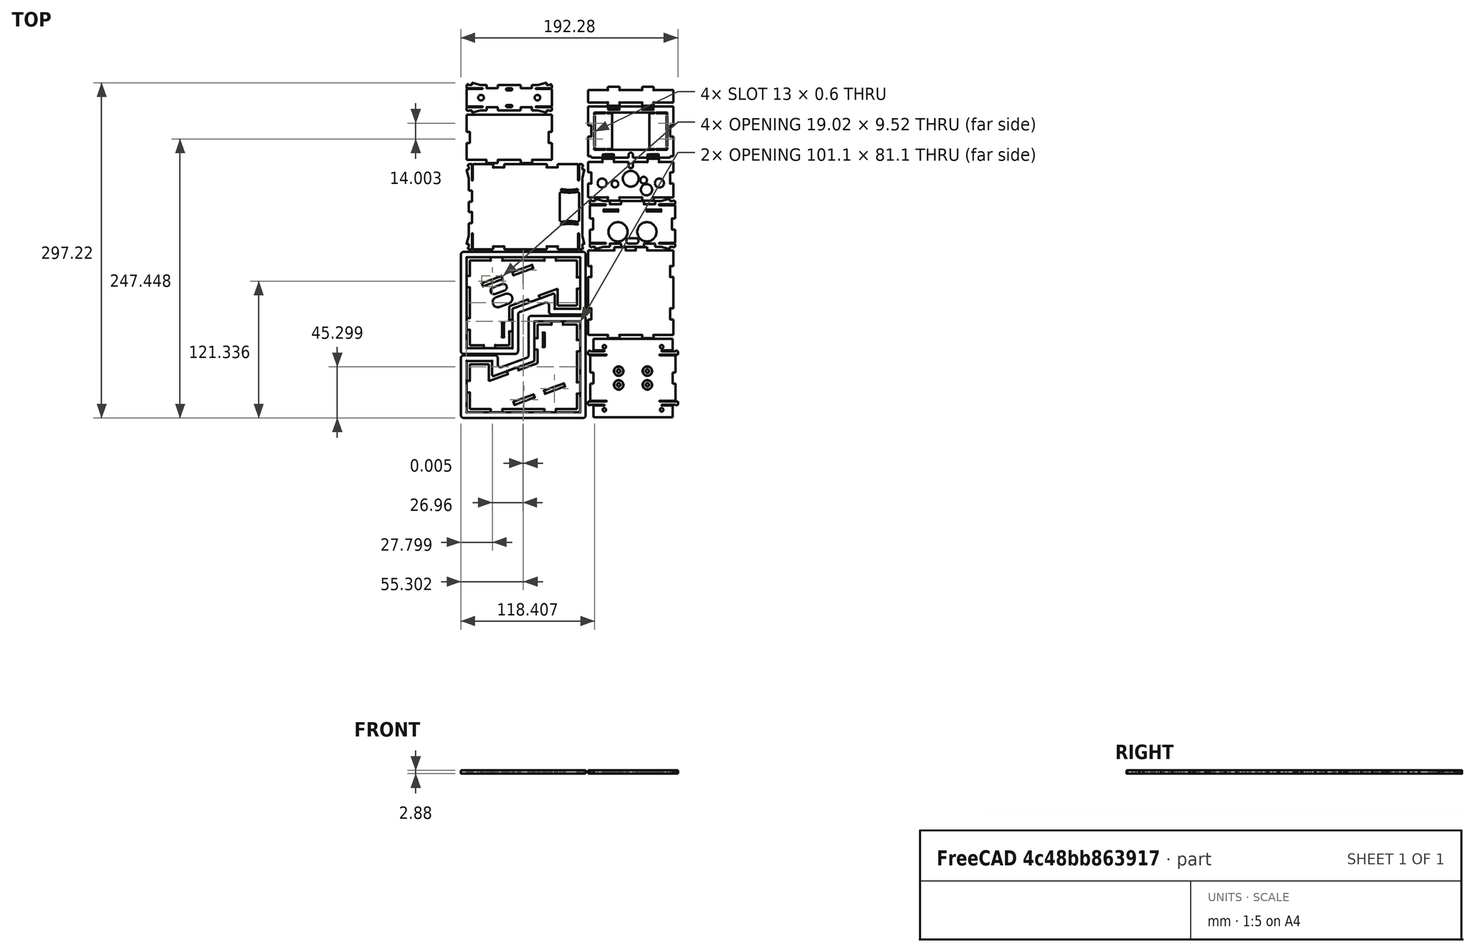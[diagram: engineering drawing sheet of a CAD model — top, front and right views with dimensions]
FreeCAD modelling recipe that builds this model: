
FCSTD DOCUMENT  (FreeCAD 1.0R39109 (Git))
Label: TheThing_v5_tabs_export
License: All rights reserved
LicenseURL: http://www.ohwr.org/attachments/2388/cern_ohl_v_1_2.txt
objects: Part::Part2DObjectPython×14, Part::Feature×13, Sketcher::SketchObject×1
note: 29 computed .brp shape members not serialized (recipe doc carries the construction recipe); baked Part::Feature solids carry a one-line shape summary decoded from their .brp

FEATURE [Part::Feature] test
  Placement = pos=(0,0,0) rot=(0,1,0;1.5708rad)
  shape: bbox 100.6 x 80.6 x 2.8 mm, 106 faces (baked)
FEATURE [Part::Feature] test001
  Placement = pos=(25.655,-97,-72.8) rot=(0.707107,0,-0.707107;3.14159rad)
  shape: bbox 100.6 x 80.6 x 2.8 mm, 96 faces (baked)
FEATURE [Part::Feature] test002
  Placement = pos=(110,-87,-32.2) rot=(-0.939693,0,0;1.22173rad)
  shape: bbox 79.6 x 69.38 x 2.8 mm, 110 faces (baked)
FEATURE [Part::Feature] test003
  Placement = pos=(0.33,129.2,25.33) rot=(0,-1,0;3.14159rad)
  shape: bbox 75.6 x 42.8 x 2.8 mm, 30 faces (baked)
FEATURE [Part::Feature] test004
  Placement = pos=(108,9,-0.3) rot=(0,0,1;0rad)
  shape: bbox 75.6 x 80.6 x 2.8 mm, 54 faces (baked)
FEATURE [Part::Feature] test005
  Placement = pos=(108,131,-38.1) rot=(0,0,1;0rad)
  shape: bbox 75.6 x 36.97 x 2.8 mm, 52 faces (baked)
FEATURE [Part::Feature] test006
  Placement = pos=(108,146,5.5) rot=(1,0,0;3.14159rad)
  shape: bbox 75.6 x 16.6 x 2.8 mm, 30 faces (baked)
FEATURE [Part::Feature] test007
  Placement = pos=(1.86,65,-55.2) rot=(0.57735,0.57735,0.57735;2.0944rad)
  shape: bbox 104.4 x 75.6 x 2.8 mm, 112 faces (baked)
FEATURE [Part::Feature] test008
  Placement = pos=(109.5,67,22.6) rot=(0,0.707107,0.707107;3.14159rad)
  shape: bbox 75.6 x 44.36 x 2.8 mm, 116 faces (baked)
FEATURE [Part::Feature] test009
  Placement = pos=(0.3,110,-60.36) rot=(-1,0,0;1.5708rad)
  shape: bbox 75.6 x 26.36 x 2.8 mm, 92 faces (baked)
FEATURE [Part::Feature] test010
  Placement = pos=(108,117,-59.7) rot=(-0.939693,0,0;1.22173rad)
  shape: bbox 75.6 x 45.69 x 2.923 mm, 114 faces (baked)
FEATURE [Part::Feature] test011
  Placement = pos=(0,0,-2) rot=(0,-1,0;4.71239rad)
  shape: bbox 110.6 x 90.6 x 2.8 mm, 46 faces (baked)
FEATURE [Part::Feature] test012
  Placement = pos=(25.65,-97,-2) rot=(0.707107,0,-0.707107;3.14159rad)
  shape: bbox 110.6 x 90.6 x 2.8 mm, 46 faces (baked)
FEATURE [Part::Part2DObjectPython] Shape2DView  # Draft 2D object (typed FeaturePython)
  AutoUpdate = true
  Base = -> test
  Clip = false
  FuseArch = false
  HiddenLines = false
  InPlace = true
  OnlySolids = false
  Projection = (0,0,1)
  ProjectionMode = 0
  SegmentLength = 0.05
  Tessellation = false
  VisibleOnly = false
FEATURE [Part::Part2DObjectPython] Shape2DView001  # Draft 2D object (typed FeaturePython)
  AutoUpdate = true
  Base = -> test001
  Clip = false
  FuseArch = false
  HiddenLines = false
  InPlace = true
  OnlySolids = false
  Projection = (0,0,1)
  ProjectionMode = 0
  SegmentLength = 0.05
  Tessellation = false
  VisibleOnly = false
FEATURE [Part::Part2DObjectPython] Shape2DView002  # Draft 2D object (typed FeaturePython)
  AutoUpdate = true
  Base = -> test002
  Clip = false
  FuseArch = false
  HiddenLines = false
  InPlace = true
  OnlySolids = false
  Projection = (0,0,1)
  ProjectionMode = 0
  SegmentLength = 0.05
  Tessellation = false
  VisibleOnly = false
FEATURE [Part::Part2DObjectPython] Shape2DView003  # Draft 2D object (typed FeaturePython)
  AutoUpdate = true
  Base = -> test003
  Clip = false
  FuseArch = false
  HiddenLines = false
  InPlace = true
  OnlySolids = false
  Projection = (0,0,1)
  ProjectionMode = 0
  SegmentLength = 0.05
  Tessellation = false
  VisibleOnly = false
FEATURE [Part::Part2DObjectPython] Shape2DView004  # Draft 2D object (typed FeaturePython)
  AutoUpdate = true
  Base = -> test004
  Clip = false
  FuseArch = false
  HiddenLines = false
  InPlace = true
  OnlySolids = false
  Projection = (0,0,1)
  ProjectionMode = 0
  SegmentLength = 0.05
  Tessellation = false
  VisibleOnly = false
FEATURE [Part::Part2DObjectPython] Shape2DView005  # Draft 2D object (typed FeaturePython)
  AutoUpdate = true
  Base = -> test005
  Clip = false
  FuseArch = false
  HiddenLines = false
  InPlace = true
  OnlySolids = false
  Projection = (0,0,1)
  ProjectionMode = 0
  SegmentLength = 0.05
  Tessellation = false
  VisibleOnly = false
FEATURE [Part::Part2DObjectPython] Shape2DView006  # Draft 2D object (typed FeaturePython)
  AutoUpdate = true
  Base = -> test006
  Clip = false
  FuseArch = false
  HiddenLines = false
  InPlace = true
  OnlySolids = false
  Projection = (0,0,1)
  ProjectionMode = 0
  SegmentLength = 0.05
  Tessellation = false
  VisibleOnly = false
FEATURE [Part::Part2DObjectPython] Shape2DView007  # Draft 2D object (typed FeaturePython)
  AutoUpdate = true
  Base = -> test007
  Clip = false
  FuseArch = false
  HiddenLines = false
  InPlace = true
  OnlySolids = false
  Projection = (0,0,1)
  ProjectionMode = 0
  SegmentLength = 0.05
  Tessellation = false
  VisibleOnly = false
FEATURE [Part::Part2DObjectPython] Shape2DView008  # Draft 2D object (typed FeaturePython)
  AutoUpdate = true
  Base = -> test008
  Clip = false
  FuseArch = false
  HiddenLines = false
  InPlace = true
  OnlySolids = false
  Projection = (0,0,1)
  ProjectionMode = 0
  SegmentLength = 0.05
  Tessellation = false
  VisibleOnly = false
FEATURE [Part::Part2DObjectPython] Shape2DView009  # Draft 2D object (typed FeaturePython)
  AutoUpdate = true
  Base = -> test009
  Clip = false
  FuseArch = false
  HiddenLines = false
  InPlace = true
  OnlySolids = false
  Projection = (0,0,1)
  ProjectionMode = 0
  SegmentLength = 0.05
  Tessellation = false
  VisibleOnly = false
FEATURE [Part::Part2DObjectPython] Shape2DView010  # Draft 2D object (typed FeaturePython)
  AutoUpdate = true
  Base = -> test010
  Clip = false
  FuseArch = false
  HiddenLines = false
  InPlace = true
  OnlySolids = false
  Projection = (0,0,1)
  ProjectionMode = 0
  SegmentLength = 0.05
  Tessellation = false
  VisibleOnly = false
FEATURE [Part::Part2DObjectPython] Shape2DView011  # Draft 2D object (typed FeaturePython)
  AutoUpdate = true
  Base = -> test011
  Clip = false
  FuseArch = false
  HiddenLines = false
  InPlace = true
  OnlySolids = false
  Projection = (0,0,1)
  ProjectionMode = 0
  SegmentLength = 0.05
  Tessellation = false
  VisibleOnly = false
FEATURE [Part::Part2DObjectPython] Shape2DView012  # Draft 2D object (typed FeaturePython)
  AutoUpdate = true
  Base = -> test012
  Clip = false
  FuseArch = false
  HiddenLines = false
  InPlace = true
  OnlySolids = false
  Projection = (0,0,1)
  ProjectionMode = 0
  SegmentLength = 0.05
  Tessellation = false
  VisibleOnly = false
FEATURE [Sketcher::SketchObject] Sketch
  ArcFitTolerance = 1e-06
  FullyConstrained = true
  MakeInternals = false
  sketch-geometry (104):
    g0: LineSegment StartX=70.2 StartY=225.92 StartZ=0 EndX=87.9733 EndY=225.92 EndZ=0
    g1: LineSegment StartX=97.7866 StartY=225.92 StartZ=0 EndX=118.213 EndY=225.92 EndZ=0
    g2: LineSegment StartX=128.027 StartY=225.92 StartZ=0 EndX=145.8 EndY=225.92 EndZ=0
    g3: LineSegment StartX=73 StartY=181.92 StartZ=0 EndX=70.2 EndY=181.92 EndZ=0
    g4: LineSegment StartX=73 StartY=180.52 StartZ=0 EndX=73 EndY=181.92 EndZ=0
    g5: LineSegment StartX=83.1933 StartY=180.52 StartZ=0 EndX=73 EndY=180.52 EndZ=0
    g6: LineSegment StartX=83.1933 StartY=180.52 StartZ=0 EndX=83.1933 EndY=183.089 EndZ=0
    g7: LineSegment StartX=83.4641 StartY=183.37 StartZ=0 EndX=92.7432 EndY=183.37 EndZ=0
    g8: LineSegment StartX=93.0066 StartY=180.52 StartZ=0 EndX=93.0066 EndY=183.089 EndZ=0
    g9: LineSegment StartX=106 StartY=180.52 StartZ=0 EndX=93.0066 EndY=180.52 EndZ=0
    g10: LineSegment StartX=106 StartY=183.02 StartZ=0 EndX=106 EndY=180.52 EndZ=0
    g11: ArcOfCircle CenterX=108 CenterY=183.02 CenterZ=0 NormalX=0 NormalY=0 NormalZ=1 AngleXU=0 Radius=2 StartAngle=0 EndAngle=3.14159
    g12: LineSegment StartX=110 StartY=180.52 StartZ=0 EndX=110 EndY=183.02 EndZ=0
    g13: LineSegment StartX=122.993 StartY=180.52 StartZ=0 EndX=110 EndY=180.52 EndZ=0
    g14: LineSegment StartX=122.993 StartY=180.52 StartZ=0 EndX=122.993 EndY=183.089 EndZ=0
    g15: LineSegment StartX=123.264 StartY=183.37 StartZ=0 EndX=132.536 EndY=183.37 EndZ=0
    g16: LineSegment StartX=132.807 StartY=180.52 StartZ=0 EndX=132.807 EndY=183.089 EndZ=0
    g17: LineSegment StartX=143 StartY=180.52 StartZ=0 EndX=132.807 EndY=180.52 EndZ=0
    g18: LineSegment StartX=143 StartY=181.92 StartZ=0 EndX=143 EndY=180.52 EndZ=0
    g19: LineSegment StartX=145.8 StartY=181.92 StartZ=0 EndX=143 EndY=181.92 EndZ=0
    g20: LineSegment StartX=145.8 StartY=199.333 StartZ=0 EndX=145.8 EndY=181.92 EndZ=0
    g21: LineSegment StartX=143.225 StartY=199.333 StartZ=0 EndX=145.8 EndY=199.333 EndZ=0
    g22: ArcOfCircle CenterX=143.053 CenterY=199.432 CenterZ=0 NormalX=0 NormalY=0 NormalZ=1 AngleXU=0 Radius=0.19911 StartAngle=2.0944 EndAngle=5.75959
    g23: LineSegment StartX=142.953 StartY=208.874 StartZ=0 EndX=142.953 EndY=199.605 EndZ=0
    g24: ArcOfCircle CenterX=143.053 CenterY=209.046 CenterZ=0 NormalX=0 NormalY=0 NormalZ=1 AngleXU=0 Radius=0.19911 StartAngle=0.5236 EndAngle=4.18879
    g25: LineSegment StartX=143.225 StartY=209.146 StartZ=0 EndX=145.8 EndY=209.146 EndZ=0
    g26: LineSegment StartX=145.8 StartY=225.92 StartZ=0 EndX=145.8 EndY=209.146 EndZ=0
    g27: LineSegment StartX=128.027 StartY=225.92 StartZ=0 EndX=128.027 EndY=223.36 EndZ=0
    g28: LineSegment StartX=118.514 StartY=223.12 StartZ=0 EndX=127.726 EndY=223.12 EndZ=0
    g29: LineSegment StartX=118.213 StartY=225.92 StartZ=0 EndX=118.213 EndY=223.36 EndZ=0
    g30: LineSegment StartX=97.7866 StartY=225.92 StartZ=0 EndX=97.7866 EndY=223.36 EndZ=0
    g31: LineSegment StartX=88.274 StartY=223.121 StartZ=0 EndX=97.486 EndY=223.121 EndZ=0
    g32: LineSegment StartX=87.9733 StartY=225.92 StartZ=0 EndX=87.9733 EndY=223.36 EndZ=0
    g33: LineSegment StartX=70.2 StartY=209.146 StartZ=0 EndX=70.2 EndY=225.92 EndZ=0
    g34: LineSegment StartX=70.2 StartY=209.146 StartZ=0 EndX=72.7636 EndY=209.146 EndZ=0
    g35: LineSegment StartX=73.0466 StartY=208.863 StartZ=0 EndX=73.0466 EndY=199.627 EndZ=0
    g36: LineSegment StartX=70.2 StartY=199.333 StartZ=0 EndX=72.7747 EndY=199.333 EndZ=0
    g37: LineSegment StartX=70.2 StartY=181.92 StartZ=0 EndX=70.2 EndY=199.333 EndZ=0
    g38: ArcOfCircle CenterX=75.927 CenterY=188.039 CenterZ=0 NormalX=0 NormalY=0 NormalZ=1 AngleXU=-9e-16 Radius=0.3 StartAngle=3.14159 EndAngle=4.71239
    g39: LineSegment StartX=75.927 StartY=187.739 StartZ=0 EndX=85.3256 EndY=187.739 EndZ=0
    g40: LineSegment StartX=75.627 StartY=189.438 StartZ=0 EndX=75.627 EndY=188.039 EndZ=0
    g41: ArcOfCircle CenterX=85.3256 CenterY=188.039 CenterZ=0 NormalX=0 NormalY=0 NormalZ=1 AngleXU=-9e-16 Radius=0.3 StartAngle=4.71239 EndAngle=7.85398
    g42: ArcOfCircle CenterX=75.927 CenterY=189.438 CenterZ=0 NormalX=0 NormalY=0 NormalZ=1 AngleXU=-9e-16 Radius=0.3 StartAngle=-5.3e-15 EndAngle=3.14159
    g43: LineSegment StartX=85.3256 StartY=188.339 StartZ=0 EndX=76.227 EndY=188.339 EndZ=0
    g44: LineSegment StartX=76.227 StartY=188.339 StartZ=0 EndX=76.227 EndY=189.438 EndZ=0
    g45: ArcOfCircle CenterX=75.927 CenterY=191.038 CenterZ=0 NormalX=0 NormalY=0 NormalZ=1 AngleXU=-9e-16 Radius=0.3 StartAngle=3.14159 EndAngle=6.28319
    g46: LineSegment StartX=76.227 StartY=191.038 StartZ=0 EndX=76.227 EndY=203.438 EndZ=0
    g47: LineSegment StartX=75.627 StartY=191.038 StartZ=0 EndX=75.627 EndY=203.438 EndZ=0
    g48: ArcOfCircle CenterX=75.927 CenterY=203.438 CenterZ=0 NormalX=0 NormalY=0 NormalZ=1 AngleXU=-9e-16 Radius=0.3 StartAngle=-3.6e-15 EndAngle=3.14159
    g49: LineSegment StartX=76.227 StartY=217.441 StartZ=0 EndX=76.227 EndY=205.041 EndZ=0
    g50: ArcOfCircle CenterX=75.927 CenterY=217.441 CenterZ=0 NormalX=0 NormalY=0 NormalZ=1 AngleXU=0 Radius=0.3 StartAngle=-4.4e-15 EndAngle=3.14159
    g51: ArcOfCircle CenterX=75.927 CenterY=205.041 CenterZ=0 NormalX=0 NormalY=0 NormalZ=1 AngleXU=0 Radius=0.3 StartAngle=3.14159 EndAngle=6.28319
    g52: LineSegment StartX=75.627 StartY=217.441 StartZ=0 EndX=75.627 EndY=205.041 EndZ=0
    g53: LineSegment StartX=75.927 StartY=220.739 StartZ=0 EndX=85.3256 EndY=220.739 EndZ=0
    g54: ArcOfCircle CenterX=75.927 CenterY=220.439 CenterZ=0 NormalX=0 NormalY=0 NormalZ=1 AngleXU=0 Radius=0.3 StartAngle=1.5708 EndAngle=3.14159
    g55: ArcOfCircle CenterX=85.3256 CenterY=220.439 CenterZ=0 NormalX=0 NormalY=0 NormalZ=1 AngleXU=0 Radius=0.3 StartAngle=4.71239 EndAngle=7.85398
    g56: LineSegment StartX=75.627 StartY=219.041 StartZ=0 EndX=75.627 EndY=220.439 EndZ=0
    g57: LineSegment StartX=85.3256 StartY=220.139 StartZ=0 EndX=76.227 EndY=220.139 EndZ=0
    g58: ArcOfCircle CenterX=75.927 CenterY=219.041 CenterZ=0 NormalX=0 NormalY=0 NormalZ=1 AngleXU=0 Radius=0.3 StartAngle=3.14159 EndAngle=6.28319
    g59: LineSegment StartX=76.227 StartY=220.139 StartZ=0 EndX=76.227 EndY=219.041 EndZ=0
    g60: ArcOfCircle CenterX=129.074 CenterY=220.439 CenterZ=0 NormalX=0 NormalY=0 NormalZ=1 AngleXU=-3.14159 Radius=0.3 StartAngle=1.5708 EndAngle=4.71239
    g61: LineSegment StartX=86.9256 StartY=220.739 StartZ=0 EndX=129.074 EndY=220.739 EndZ=0
    g62: LineSegment StartX=124.501 StartY=220.139 StartZ=0 EndX=129.074 EndY=220.139 EndZ=0
    g63: ArcOfCircle CenterX=86.9256 CenterY=220.439 CenterZ=0 NormalX=0 NormalY=0 NormalZ=1 AngleXU=0 Radius=0.3 StartAngle=1.5708 EndAngle=4.71239
    g64: LineSegment StartX=124.501 StartY=220.139 StartZ=0 EndX=124.501 EndY=188.339 EndZ=0
    g65: LineSegment StartX=91.4993 StartY=220.139 StartZ=0 EndX=86.9256 EndY=220.139 EndZ=0
    g66: LineSegment StartX=124.501 StartY=188.339 StartZ=0 EndX=129.074 EndY=188.339 EndZ=0
    g67: LineSegment StartX=91.4993 StartY=188.339 StartZ=0 EndX=91.4993 EndY=220.139 EndZ=0
    g68: ArcOfCircle CenterX=129.074 CenterY=188.039 CenterZ=0 NormalX=0 NormalY=0 NormalZ=1 AngleXU=3.14159 Radius=0.3 StartAngle=1.5708 EndAngle=4.71239
    g69: LineSegment StartX=91.4993 StartY=188.339 StartZ=0 EndX=86.9256 EndY=188.339 EndZ=0
    g70: LineSegment StartX=129.074 StartY=187.739 StartZ=0 EndX=86.9256 EndY=187.739 EndZ=0
    g71: ArcOfCircle CenterX=86.9256 CenterY=188.039 CenterZ=0 NormalX=0 NormalY=0 NormalZ=1 AngleXU=-9e-16 Radius=0.3 StartAngle=1.5708 EndAngle=4.71239
    g72: LineSegment StartX=140.073 StartY=187.739 StartZ=0 EndX=130.674 EndY=187.739 EndZ=0
    g73: ArcOfCircle CenterX=140.073 CenterY=188.039 CenterZ=0 NormalX=0 NormalY=0 NormalZ=1 AngleXU=3.14159 Radius=0.3 StartAngle=1.5708 EndAngle=3.14159
    g74: ArcOfCircle CenterX=130.674 CenterY=188.039 CenterZ=0 NormalX=0 NormalY=0 NormalZ=1 AngleXU=3.14159 Radius=0.3 StartAngle=4.71239 EndAngle=7.85398
    g75: LineSegment StartX=140.373 StartY=189.438 StartZ=0 EndX=140.373 EndY=188.039 EndZ=0
    g76: LineSegment StartX=130.674 StartY=188.339 StartZ=0 EndX=139.773 EndY=188.339 EndZ=0
    g77: ArcOfCircle CenterX=140.073 CenterY=189.438 CenterZ=0 NormalX=0 NormalY=0 NormalZ=1 AngleXU=3.14159 Radius=0.3 StartAngle=3.14159 EndAngle=6.28319
    g78: LineSegment StartX=139.773 StartY=188.339 StartZ=0 EndX=139.773 EndY=189.438 EndZ=0
    g79: LineSegment StartX=139.773 StartY=191.038 StartZ=0 EndX=139.773 EndY=203.438 EndZ=0
    g80: ArcOfCircle CenterX=140.073 CenterY=191.038 CenterZ=0 NormalX=0 NormalY=0 NormalZ=1 AngleXU=3.14159 Radius=0.3 StartAngle=-4.4e-15 EndAngle=3.14159
    g81: ArcOfCircle CenterX=140.073 CenterY=203.438 CenterZ=0 NormalX=0 NormalY=0 NormalZ=1 AngleXU=3.14159 Radius=0.3 StartAngle=3.14159 EndAngle=6.28319
    g82: LineSegment StartX=140.373 StartY=191.038 StartZ=0 EndX=140.373 EndY=203.438 EndZ=0
    g83: ArcOfCircle CenterX=140.073 CenterY=217.441 CenterZ=0 NormalX=0 NormalY=0 NormalZ=1 AngleXU=-3.14159 Radius=0.3 StartAngle=3.14159 EndAngle=6.28319
    g84: LineSegment StartX=139.773 StartY=217.441 StartZ=0 EndX=139.773 EndY=205.041 EndZ=0
    g85: LineSegment StartX=140.373 StartY=217.441 StartZ=0 EndX=140.373 EndY=205.041 EndZ=0
    g86: ArcOfCircle CenterX=140.073 CenterY=205.041 CenterZ=0 NormalX=0 NormalY=0 NormalZ=1 AngleXU=-3.14159 Radius=0.3 StartAngle=-3.6e-15 EndAngle=3.14159
    g87: ArcOfCircle CenterX=140.073 CenterY=220.439 CenterZ=0 NormalX=0 NormalY=0 NormalZ=1 AngleXU=-3.14159 Radius=0.3 StartAngle=3.14159 EndAngle=4.71239
    g88: LineSegment StartX=140.073 StartY=220.739 StartZ=0 EndX=130.674 EndY=220.739 EndZ=0
    g89: LineSegment StartX=140.373 StartY=219.041 StartZ=0 EndX=140.373 EndY=220.439 EndZ=0
    g90: ArcOfCircle CenterX=130.674 CenterY=220.439 CenterZ=0 NormalX=0 NormalY=0 NormalZ=1 AngleXU=-3.14159 Radius=0.3 StartAngle=4.71239 EndAngle=7.85398
    g91: ArcOfCircle CenterX=140.073 CenterY=219.041 CenterZ=0 NormalX=0 NormalY=0 NormalZ=1 AngleXU=-3.14159 Radius=0.3 StartAngle=-5.3e-15 EndAngle=3.14159
    g92: LineSegment StartX=130.674 StartY=220.139 StartZ=0 EndX=139.773 EndY=220.139 EndZ=0
    g93: LineSegment StartX=139.773 StartY=220.139 StartZ=0 EndX=139.773 EndY=219.041 EndZ=0
    g94: ArcOfCircle CenterX=97.6871 CenterY=223.177 CenterZ=0 NormalX=0 NormalY=0 NormalZ=1 AngleXU=0 Radius=0.208767 StartAngle=3.41408 EndAngle=7.35689
    g95: ArcOfCircle CenterX=88.0729 CenterY=223.177 CenterZ=0 NormalX=0 NormalY=0 NormalZ=1 AngleXU=0 Radius=0.208767 StartAngle=2.06789 EndAngle=6.0107
    g96: ArcOfCircle CenterX=118.313 CenterY=223.177 CenterZ=0 NormalX=0 NormalY=0 NormalZ=1 AngleXU=0 Radius=0.208767 StartAngle=2.06789 EndAngle=6.00866
    g97: ArcOfCircle CenterX=127.927 CenterY=223.177 CenterZ=0 NormalX=0 NormalY=0 NormalZ=1 AngleXU=0 Radius=0.208767 StartAngle=3.41612 EndAngle=7.35689
    g98: ArcOfCircle CenterX=72.9471 CenterY=209.046 CenterZ=0 NormalX=0 NormalY=0 NormalZ=1 AngleXU=0 Radius=0.208767 StartAngle=5.20948 EndAngle=8.92769
    g99: ArcOfCircle CenterX=72.9541 CenterY=199.439 CenterZ=0 NormalX=0 NormalY=0 NormalZ=1 AngleXU=0 Radius=0.208767 StartAngle=3.67768 EndAngle=7.39491
    g100: ArcOfCircle CenterX=83.2898 CenterY=183.267 CenterZ=0 NormalX=0 NormalY=0 NormalZ=1 AngleXU=0 Radius=0.202242 StartAngle=0.532255 EndAngle=4.2153
    g101: ArcOfCircle CenterX=92.9102 CenterY=183.263 CenterZ=0 NormalX=0 NormalY=0 NormalZ=1 AngleXU=0 Radius=0.19839 StartAngle=5.22004 EndAngle=8.85496
    g102: ArcOfCircle CenterX=123.09 CenterY=183.267 CenterZ=0 NormalX=0 NormalY=0 NormalZ=1 AngleXU=0 Radius=0.202242 StartAngle=0.532259 EndAngle=4.2153
    g103: ArcOfCircle CenterX=132.71 CenterY=183.267 CenterZ=0 NormalX=0 NormalY=0 NormalZ=1 AngleXU=0 Radius=0.202242 StartAngle=5.20948 EndAngle=8.89252
  constraints (299):
    c: Coincident(g2,g27)
    c: Coincident(g2,g26)
    c: Coincident(g25,g26)
    c: Coincident(g24,g25)
    c: Coincident(g23,g24)
    c: Coincident(g22,g23)
    c: Coincident(g21,g22)
    c: Coincident(g20,g21)
    c: Coincident(g19,g20)
    c: Coincident(g18,g19)
    c: Coincident(g17,g18)
    c: Coincident(g12,g13)
    c: Coincident(g9,g10)
    c: Coincident(g4,g5)
    c: Coincident(g3,g4)
    c: Coincident(g3,g37)
    c: Coincident(g36,g37)
    c: Coincident(g33,g34)
    c: Coincident(g0,g33)
    c: Coincident(g0,g32)
    c: Coincident(g1,g30)
    c: Coincident(g1,g29)
    c: Vertical(g27)
    c: Horizontal(g2)
    c: Vertical(g26)
    c: Horizontal(g25)
    c: Vertical(g23)
    c: Horizontal(g21)
    c: Vertical(g20)
    c: Horizontal(g19)
    c: Vertical(g18)
    c: Horizontal(g17)
    c: Vertical(g16)
    c: Horizontal(g15)
    c: Vertical(g14)
    c: Horizontal(g13)
    c: Vertical(g12)
    c: Vertical(g10)
    c: Horizontal(g9)
    c: Vertical(g8)
    c: Horizontal(g7)
    c: Vertical(g6)
    c: Horizontal(g5)
    c: Vertical(g4)
    c: Horizontal(g3)
    c: Vertical(g37)
    c: Horizontal(g36)
    c: Vertical(g35)
    c: Horizontal(g34)
    c: Vertical(g33)
    c: Horizontal(g0)
    c: Vertical(g32)
    c: Horizontal(g31)
    c: Vertical(g30)
    c: Horizontal(g1)
    c: Vertical(g29)
    c: Horizontal(g28)
    c: Vertical(g56)
    c: Vertical(g59)
    c: Horizontal(g57)
    c: Horizontal(g53)
    c: Horizontal(g65)
    c: Horizontal(g61)
    c: Vertical(g67)
    c: Horizontal(g62)
    c: Vertical(g64)
    c: Horizontal(g88)
    c: Horizontal(g92)
    c: Vertical(g93)
    c: Vertical(g89)
    c: Vertical(g84)
    c: Vertical(g85)
    c: Vertical(g79)
    c: Vertical(g82)
    c: Vertical(g78)
    c: Vertical(g75)
    c: Horizontal(g76)
    c: Horizontal(g72)
    c: Horizontal(g66)
    c: Horizontal(g70)
    c: Horizontal(g69)
    c: Horizontal(g43)
    c: Horizontal(g39)
    c: Vertical(g44)
    c: Vertical(g40)
    c: Vertical(g47)
    c: Vertical(g46)
    c: Vertical(g49)
    c: Vertical(g52)
    c: Coincident(g57,g59)
    c: Coincident(g62,g64)
    c: Coincident(g64,g66)
    c: Coincident(g67,g69)
    c: Coincident(g65,g67)
    c: Coincident(g92,g93)
    c: Coincident(g76,g78)
    c: Coincident(g43,g44)
    c: DistanceX(g58) = 75.927
    c: DistanceY(g58) = 219.041
    c: DistanceX(g54) = 75.927
    c: DistanceY(g54) = 220.439
    c: DistanceX(g55) = 85.3256
    c: DistanceY(g55) = 220.439
    c: DistanceX(g63) = 86.9256
    c: DistanceY(g63) = 220.439
    c: DistanceX(g60) = 129.074
    c: DistanceY(g60) = 220.439
    c: DistanceX(g90) = 130.674
    c: DistanceY(g90) = 220.439
    c: DistanceX(g87) = 140.073
    c: DistanceY(g87) = 220.439
    c: DistanceX(g91) = 140.073
    c: DistanceY(g91) = 219.041
    c: DistanceX(g83) = 140.073
    c: DistanceY(g83) = 217.441
    c: DistanceX(g81) = 140.073
    c: DistanceY(g81) = 203.438
    c: DistanceX(g77) = 140.073
    c: DistanceY(g77) = 189.438
    c: DistanceX(g73) = 140.073
    c: DistanceY(g73) = 188.039
    c: DistanceX(g74) = 130.674
    c: DistanceY(g74) = 188.039
    c: DistanceX(g68) = 129.074
    c: DistanceY(g68) = 188.039
    c: DistanceX(g11) = 108
    c: DistanceY(g11) = 183.02
    c: DistanceX(g71) = 86.9256
    c: DistanceY(g71) = 188.039
    c: DistanceX(g41) = 85.3256
    c: DistanceY(g41) = 188.039
    c: DistanceX(g38) = 75.927
    c: DistanceY(g38) = 188.039
    c: DistanceX(g42) = 75.927
    c: DistanceY(g42) = 189.438
    c: DistanceX(g45) = 75.927
    c: DistanceY(g45) = 191.038
    c: DistanceX(g51) = 75.927
    c: DistanceY(g51) = 205.041
    c: DistanceX(g0) = 70.2
    c: DistanceY(g0) = 225.92
    c: DistanceX(g32) = 87.9733
    c: DistanceY(g32) = 223.36
    c: DistanceX(g30) = 97.7866
    c: DistanceY(g30) = 223.36
    c: DistanceX(g1) = 118.213
    c: DistanceY(g1) = 225.92
    c: DistanceX(g27) = 128.027
    c: DistanceY(g27) = 223.36
    c: DistanceX(g2) = 145.8
    c: DistanceY(g2) = 225.92
    c: DistanceX(g24) = 143.225
    c: DistanceY(g24) = 209.146
    c: DistanceX(g24) = 143.053
    c: DistanceY(g24) = 209.046
    c: DistanceX(g22) = 142.953
    c: DistanceY(g22) = 199.605
    c: DistanceX(g22) = 143.053
    c: DistanceY(g22) = 199.432
    c: DistanceX(g20) = 145.8
    c: DistanceY(g20) = 199.333
    c: DistanceX(g18) = 143
    c: DistanceY(g18) = 181.92
    c: DistanceX(g16) = 132.807
    c: DistanceY(g16) = 183.089
    c: DistanceX(g14) = 122.993
    c: DistanceY(g14) = 183.089
    c: DistanceX(g12) = 110
    c: DistanceY(g12) = 180.52
    c: DistanceY(g9) = 180.52
    c: DistanceX(g8) = 93.0066
    c: DistanceY(g8) = 183.089
    c: DistanceX(g7) = 92.7432
    c: DistanceY(g7) = 183.37
    c: DistanceX(g6) = 83.1933
    c: DistanceY(g6) = 183.089
    c: DistanceX(g4) = 73
    c: DistanceY(g4) = 180.52
    c: DistanceX(g3) = 70.2
    c: DistanceY(g3) = 181.92
    c: DistanceX(g36) = 72.7747
    c: DistanceY(g36) = 199.333
    c: DistanceX(g35) = 73.0466
    c: Equal(g4,g18)
    c: Equal(g33,g26)
    c: Coincident(g16,g17)
    c: Coincident(g13,g14)
    c: Tangent(g11,g12) = -1.5708
    c: Tangent(g10,g11) = -1.5708
    c: Coincident(g8,g9)
    c: Coincident(g5,g6)
    c: Tangent(g56,g58) = 1.5708
    c: Tangent(g58,g59) = 1.5708
    c: Tangent(g54,g56) = 1.5708
    c: Tangent(g53,g54) = 1.5708
    c: Tangent(g53,g55) = 1.5708
    c: Tangent(g55,g57) = 1.5708
    c: Tangent(g61,g63) = 1.5708
    c: Tangent(g63,g65) = 1.5708
    c: Tangent(g60,g61) = 1.5708
    c: Tangent(g60,g62) = -1.5708
    c: Tangent(g88,g90) = -1.5708
    c: Tangent(g90,g92) = -1.5708
    c: Tangent(g87,g88) = -1.5708
    c: Tangent(g87,g89) = -1.5708
    c: Tangent(g89,g91) = -1.5708
    c: Tangent(g91,g93) = -1.5708
    c: Tangent(g83,g84) = -1.5708
    c: Tangent(g83,g85) = 1.5708
    c: Tangent(g84,g86) = -1.5708
    c: Tangent(g85,g86) = 1.5708
    c: Tangent(g81,g82) = -1.5708
    c: Tangent(g79,g81) = 1.5708
    c: Tangent(g80,g82) = -1.5708
    c: Tangent(g79,g80) = 1.5708
    c: Tangent(g75,g77) = 1.5708
    c: Tangent(g77,g78) = 1.5708
    c: Tangent(g73,g75) = 1.5708
    c: Tangent(g72,g73) = 1.5708
    c: Tangent(g72,g74) = 1.5708
    c: Tangent(g74,g76) = 1.5708
    c: Tangent(g66,g68) = 1.5708
    c: Tangent(g68,g70) = 1.5708
    c: Tangent(g70,g71) = 1.5708
    c: Tangent(g69,g71) = -1.5708
    c: Tangent(g39,g41) = -1.5708
    c: Tangent(g41,g43) = -1.5708
    c: Tangent(g38,g39) = -1.5708
    c: Tangent(g38,g40) = -1.5708
    c: Tangent(g40,g42) = -1.5708
    c: Tangent(g42,g44) = -1.5708
    c: Tangent(g45,g46) = -1.5708
    c: Tangent(g45,g47) = 1.5708
    c: Tangent(g46,g48) = -1.5708
    c: Tangent(g47,g48) = 1.5708
    c: Tangent(g51,g52) = -1.5708
    c: Tangent(g49,g51) = 1.5708
    c: Tangent(g49,g50) = 1.5708
    c: Tangent(g50,g52) = -1.5708
    c: Equal(g55,g63)
    c: Equal(g60,g90)
    c: Equal(g91,g83)
    c: Equal(g86,g81)
    c: Equal(g80,g77)
    c: Equal(g74,g68)
    c: Equal(g71,g41)
    c: Equal(g42,g45)
    c: Equal(g48,g51)
    c: Radius(g55) = 0.3
    c: DistanceY(g50) = 217.441
    c: DistanceY(g48) = 203.438
    c: DistanceY(g80) = 191.038
    c: DistanceY(g86) = 205.041
    c: Equal(g66,g69)
    c: DistanceX(g65) = 91.4993
    c: Coincident(g94,g30)
    c: DistanceX(g94) = 97.6871
    c: DistanceY(g94) = 223.177
    c: Coincident(g31,g94)
    c: DistanceX(g95) = 88.0729
    c: DistanceY(g95) = 223.177
    c: Coincident(g31,g95)
    c: DistanceX(g31) = 97.486
    c: DistanceX(g96) = 118.313
    c: DistanceY(g96) = 223.177
    c: Equal(g96,g94)
    c: Coincident(g28,g96)
    c: Coincident(g97,g27)
    c: Coincident(g28,g97)
    c: DistanceX(g97) = 127.927
    c: DistanceY(g97) = 223.177
    c: DistanceX(g28) = 127.726
    c: DistanceX(g98) = 72.9471
    c: DistanceY(g98) = 209.046
    c: Equal(g98,g95)
    c: Coincident(g35,g98)
    c: Coincident(g34,g98)
    c: Coincident(g29,g96)
    c: Coincident(g32,g95)
    c: Coincident(g36,g99)
    c: Coincident(g35,g99)
    c: Equal(g99,g98)
    c: DistanceX(g99) = 72.9541
    c: Coincident(g100,g6)
    c: DistanceX(g100) = 83.2898
    c: DistanceY(g100) = 183.267
    c: Coincident(g7,g100)
    c: Coincident(g101,g7)
    c: DistanceX(g101) = 92.9102
    c: Coincident(g8,g101)
    c: Coincident(g102,g14)
    c: Coincident(g15,g102)
    c: DistanceX(g102) = 123.09
    c: DistanceY(g102) = 183.267
    c: Coincident(g103,g15)
    c: Coincident(g16,g103)
    c: DistanceX(g103) = 132.71
    c: DistanceY(g103) = 183.267
    c: DistanceX(g15) = 132.536
FEATURE [Part::Part2DObjectPython] Shape2DView013  # Draft 2D object (typed FeaturePython)
  AutoUpdate = true
  Base = -> Sketch
  Clip = false
  FuseArch = false
  HiddenLines = false
  InPlace = true
  OnlySolids = false
  Placement = pos=(0,-72,0) rot=(0,0,1;0rad)
  Projection = (0,0,1)
  ProjectionMode = 0
  SegmentLength = 0.05
  Tessellation = false
  VisibleOnly = false
